# Revit family: 67L-S-SQ
name_source: partatom
category: Lighting Fixtures
units: mm (PartAtom-declared; Revit-internal decimal feet)

## family parameters
Cut with Voids When Loaded = No
Host = Face
Light Source = Yes
OmniClass Number = 23.80.70.11
OmniClass Title = Luminaries for Internal Lighting
Part Type = Normal
Room Calculation Point = No
Round Connector Dimension = Use Diameter
Shared = Yes

## types (6) — shared parameters
Apparent Load = 0 VA
Assembly Code = D5020200
Color Filter = 16777215
Default Elevation = 48 "
Description = The NOTE 67L Surface brings direct illumination, performance and versatility, all within a slim profile and a fresh, contemporary style
Dimming Lamp Color Temperature Shift = <None>
Emit Shape Visible in Rendering = No
Emit from Rectangle Length = 47 "
Emit from Rectangle Width = 2 "
Frequency = 60 Hz
Lamp = LED
Load Classification = Lighting
Manufacturer = Litecontrol
Model = 67L-S-Square
Photometric Notes = Photometric web files Download in below link
Photometric Web File = 67L-S-D-4-4-BL-C1-35K-D055.IES
Power Factor = 1
Reflector Finish = White Glass
Tilt Angle = -90.00°
Type Comments = Lighting Fixture
URL = https://www.currentlighting.com
Voltage = 120 V
Wattage Comments = 550 to 1800 lumens/ft
Watts = 5 W
Width = 48 "

## per-type parameters (varying)
| type | Product Material |
| Note 67L-Textured Matte White | Paint -  Textured Matte White |
| Note 67L-Matte White | Paint -  Matte White |
| Note 67L-Light Silver | Paint - Light Silver |
| Note 67L-Machined Aluminium | Paint - Machined Aluminum |
| Note 67L-Carbon Black | Paint - Carbon Black |
| Note 67L-Textured Camera Black | Paint -  Textured Camera Black |

## geometry (parser evidence)
native form markers: Blend x2, Sweep x5
no freeform markers — native parametric forms only
